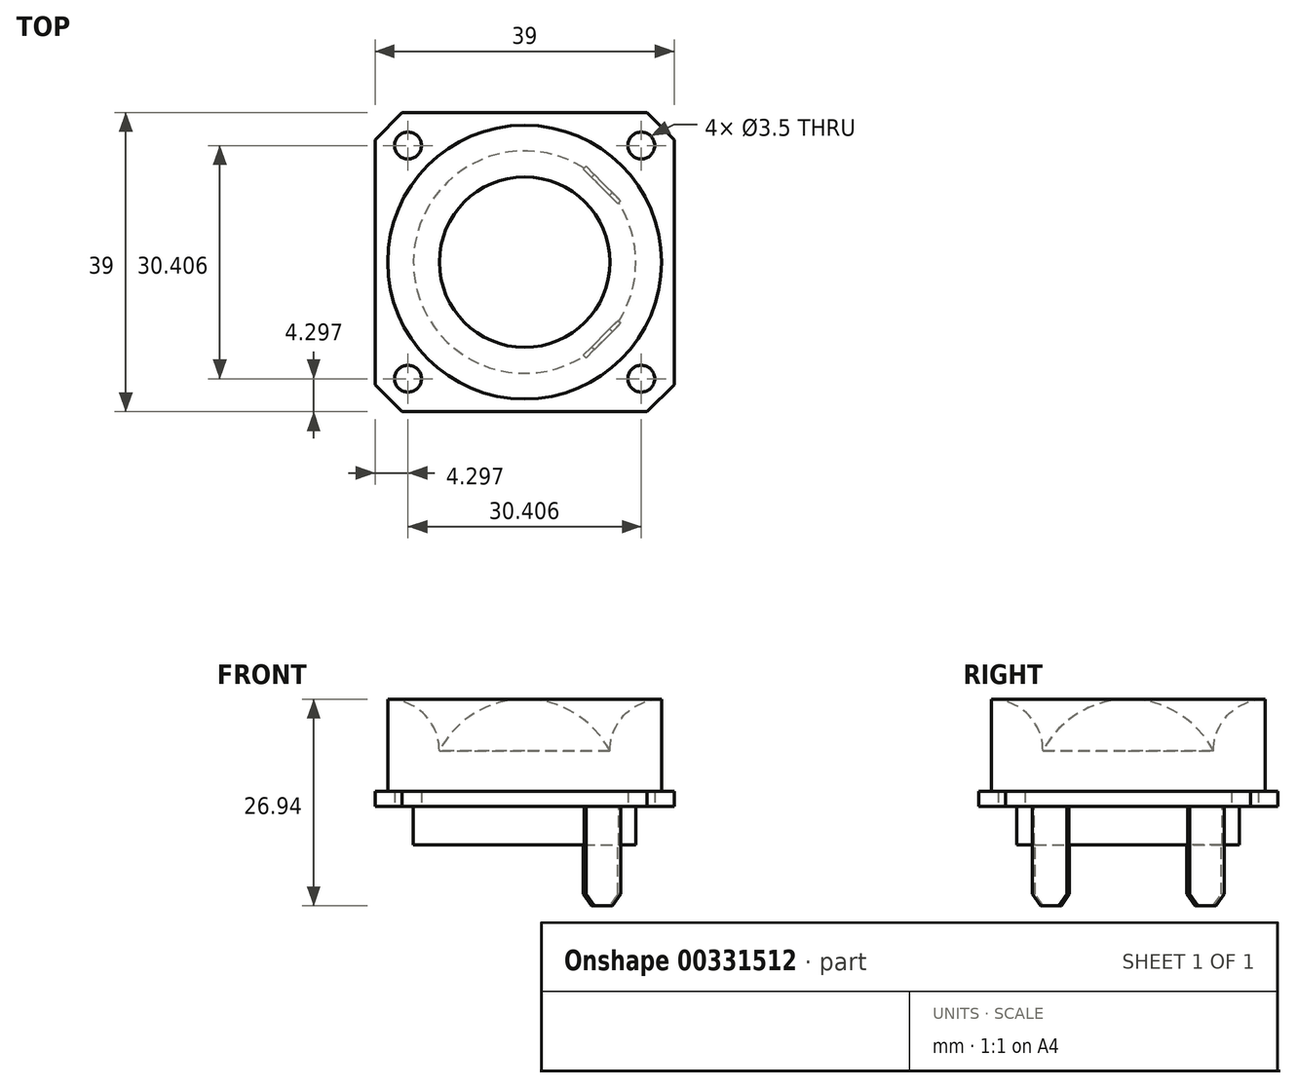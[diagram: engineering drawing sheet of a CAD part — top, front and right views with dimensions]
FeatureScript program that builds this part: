
annotation { "Feature Type Name" : "Feature", "Feature Type Description" : "" }
export const myFeature = defineFeature(function(context is Context, id is Id, definition is map)
    precondition{}
    {
        {
            var Q0;
            Q0=qCreatedBy(makeId("Right.planeOp"),FACE);
            var sketch = newSketch(context, id + "F0", { "sketchPlane" : qUnion([Q0])});
            skLineSegment(sketch, "E0", {"start": v(0, 0) * mm, "end": v(0, 18.25) * mm, "construction": true});
            skLineSegment(sketch, "E1", {"start": v(-17.85, 0) * mm, "end": v(-17.85, -14) * mm});
            skLineSegment(sketch, "E2", {"start": v(-17.85, -14) * mm, "end": v(0, -14) * mm});
            skLineSegment(sketch, "E3", {"start": v(0, -14) * mm, "end": v(0, 0) * mm});
            skArc(sketch, "E4", {"start": v(0, 0) * mm, "mid": v(-6.5, -1.82) * mm, "end": v(-11.11, -6.74) * mm});
            skArc(sketch, "E5", {"start": v(-11.11, -6.74) * mm, "mid": v(-13.09, -1.97) * mm, "end": v(-17.85, 0) * mm});
            skPoint(sketch, "E6", {"position": v(-17.85, -7) * mm});
            skSolve(sketch);
        }
        {
            var Q0;
            Q0 = qSketchRegion(id + "F0", true);
            var Q1;
            Q1=sQuery(id+"F0.wireOp",EDGE,"E0");
            revolve(context, id + "F1", {"entities" : qUnion([Q0]), "axis" : qUnion([Q1]), "revolveType" : RevolveType.FULL});
        }
        {
            var Q0;
            Q0=makeQuery(id+"F1.opRevolve","SWEPT_FACE",FACE,{"disambiguationData":[OSD([sQuery(id+"F0.wireOp",EDGE,"E2")])]});
            var sketch = newSketch(context, id + "F2", { "sketchPlane" : qUnion([Q0])});
            skLineSegment(sketch, "E7", {"start": v(0, -19.5) * mm, "end": v(15.96, -19.5) * mm});
            skLineSegment(sketch, "E8", {"start": v(15.96, -19.5) * mm, "end": v(19.5, -15.96) * mm});
            skLineSegment(sketch, "E9", {"start": v(19.5, -15.96) * mm, "end": v(19.5, 0) * mm});
            skLineSegment(sketch, "E10", {"start": v(0, 0) * mm, "end": v(0, -19.5) * mm, "construction": true});
            skLineSegment(sketch, "E11", {"start": v(0, 0) * mm, "end": v(19.5, 0) * mm, "construction": true});
            skCircle(sketch, "E12", {"center": v(15.2, -15.2) * mm, "radius": 1.75 * mm});
            skLineSegment(sketch, "E13", {"start": v(15.2, -15.2) * mm, "end": v(0, 0) * mm, "construction": true});
            skLineSegment(sketch, "E14", {"start": v(15.2, -15.2) * mm, "end": v(17.73, -17.73) * mm, "construction": true});
            skCircle(sketch, "E15.MirrorC", {"center": v(-15.2, -15.2) * mm, "radius": 1.75 * mm});
            skLineSegment(sketch, "E16.MirrorCS", {"start": v(-19.5, -15.96) * mm, "end": v(-19.5, 0) * mm});
            skLineSegment(sketch, "E17.MirrorCS", {"start": v(-15.96, -19.5) * mm, "end": v(-19.5, -15.96) * mm});
            skLineSegment(sketch, "E18.MirrorCS", {"start": v(0, -19.5) * mm, "end": v(-15.96, -19.5) * mm});
            skLineSegment(sketch, "E19.MirrorCS", {"start": v(19.5, 15.96) * mm, "end": v(19.5, 0) * mm});
            skCircle(sketch, "E20.MirrorC", {"center": v(15.2, 15.2) * mm, "radius": 1.75 * mm});
            skLineSegment(sketch, "E21.MirrorCS", {"start": v(15.96, 19.5) * mm, "end": v(19.5, 15.96) * mm});
            skLineSegment(sketch, "E22.MirrorCS", {"start": v(0, 19.5) * mm, "end": v(15.96, 19.5) * mm});
            skCircle(sketch, "E23.MirrorC", {"center": v(-15.2, 15.2) * mm, "radius": 1.75 * mm});
            skLineSegment(sketch, "E24.MirrorCS", {"start": v(-19.5, 15.96) * mm, "end": v(-19.5, 0) * mm});
            skLineSegment(sketch, "E25.MirrorCS", {"start": v(-15.96, 19.5) * mm, "end": v(-19.5, 15.96) * mm});
            skLineSegment(sketch, "E26.MirrorCS", {"start": v(0, 19.5) * mm, "end": v(-15.96, 19.5) * mm});
            skSolve(sketch);
        }
        {
            var Q0;
            Q0 = qSketchRegion(id + "F2", true);
            extrude(context, id + "F3", {"entities" : qUnion([Q0]), "operationType" : NewBodyOperationType.ADD, "oppositeDirection" : true, "depth" : 2 * mm});
        }
        {
            var Q0;
            Q0=makeQuery(id+"F3.boolean.opBoolean","MERGE",FACE,{"derivedFrom":[makeQuery(id+"F1.opRevolve","SWEPT_FACE",FACE,{"disambiguationData":[OSD([sQuery(id+"F0.wireOp",EDGE,"E2")])]}),makeQuery(id+"F3.opExtrude","CAP_FACE",FACE,{"disambiguationData":[OSD([sQuery(id+"F2.wireOp",EDGE,"E7"),sQuery(id+"F2.wireOp",EDGE,"E8"),sQuery(id+"F2.wireOp",EDGE,"E9"),sQuery(id+"F2.wireOp",EDGE,"E12"),sQuery(id+"F2.wireOp",EDGE,"E15.MirrorC"),sQuery(id+"F2.wireOp",EDGE,"E16.MirrorCS"),sQuery(id+"F2.wireOp",EDGE,"E17.MirrorCS"),sQuery(id+"F2.wireOp",EDGE,"E18.MirrorCS"),sQuery(id+"F2.wireOp",EDGE,"E19.MirrorCS"),sQuery(id+"F2.wireOp",EDGE,"E20.MirrorC"),sQuery(id+"F2.wireOp",EDGE,"E21.MirrorCS"),sQuery(id+"F2.wireOp",EDGE,"E22.MirrorCS"),sQuery(id+"F2.wireOp",EDGE,"E23.MirrorC"),sQuery(id+"F2.wireOp",EDGE,"E24.MirrorCS"),sQuery(id+"F2.wireOp",EDGE,"E25.MirrorCS"),sQuery(id+"F2.wireOp",EDGE,"E26.MirrorCS")])],"isStart":true})]});
            var sketch = newSketch(context, id + "F4", { "sketchPlane" : qUnion([Q0])});
            skCircle(sketch, "E27", {"center": v(0, 0) * mm, "radius": 14.5 * mm});
            skSolve(sketch);
        }
        {
            var Q0;
            Q0 = qSketchRegion(id + "F4", true);
            extrude(context, id + "F5", {"entities" : qUnion([Q0]), "operationType" : NewBodyOperationType.ADD, "depth" : 5 * mm});
        }
        {
            var Q0;
            Q0=makeQuery(id+"F3.boolean.opBoolean","MERGE",FACE,{"derivedFrom":[makeQuery(id+"F1.opRevolve","SWEPT_FACE",FACE,{"disambiguationData":[OSD([sQuery(id+"F0.wireOp",EDGE,"E2")])]}),makeQuery(id+"F3.opExtrude","CAP_FACE",FACE,{"disambiguationData":[OSD([sQuery(id+"F2.wireOp",EDGE,"E7"),sQuery(id+"F2.wireOp",EDGE,"E8"),sQuery(id+"F2.wireOp",EDGE,"E9"),sQuery(id+"F2.wireOp",EDGE,"E12"),sQuery(id+"F2.wireOp",EDGE,"E15.MirrorC"),sQuery(id+"F2.wireOp",EDGE,"E16.MirrorCS"),sQuery(id+"F2.wireOp",EDGE,"E17.MirrorCS"),sQuery(id+"F2.wireOp",EDGE,"E18.MirrorCS"),sQuery(id+"F2.wireOp",EDGE,"E19.MirrorCS"),sQuery(id+"F2.wireOp",EDGE,"E20.MirrorC"),sQuery(id+"F2.wireOp",EDGE,"E21.MirrorCS"),sQuery(id+"F2.wireOp",EDGE,"E22.MirrorCS"),sQuery(id+"F2.wireOp",EDGE,"E23.MirrorC"),sQuery(id+"F2.wireOp",EDGE,"E24.MirrorCS"),sQuery(id+"F2.wireOp",EDGE,"E25.MirrorCS"),sQuery(id+"F2.wireOp",EDGE,"E26.MirrorCS")])],"isStart":true})]});
            var sketch = newSketch(context, id + "F6", { "sketchPlane" : qUnion([Q0])});
            skLineSegment(sketch, "E28", {"start": v(0, 0) * mm, "end": v(13.6, 0) * mm, "construction": true});
            skLineSegment(sketch, "E29", {"start": v(8, 12.5) * mm, "end": v(12.5, 8) * mm});
            skLineSegment(sketch, "E30", {"start": v(12.14, 7.65) * mm, "end": v(12.5, 8) * mm});
            skLineSegment(sketch, "E31", {"start": v(12.14, 7.65) * mm, "end": v(7.65, 12.14) * mm});
            skLineSegment(sketch, "E32", {"start": v(8, 12.5) * mm, "end": v(7.65, 12.14) * mm});
            skPoint(sketch, "E33", {"position": v(10.25, 10.25) * mm});
            skLineSegment(sketch, "E34.MirrorCS", {"start": v(12.14, -7.65) * mm, "end": v(12.5, -8) * mm});
            skLineSegment(sketch, "E35.MirrorCS", {"start": v(12.14, -7.65) * mm, "end": v(7.65, -12.14) * mm});
            skLineSegment(sketch, "E36.MirrorCS", {"start": v(8, -12.5) * mm, "end": v(7.65, -12.14) * mm});
            skLineSegment(sketch, "E37.MirrorCS", {"start": v(8, -12.5) * mm, "end": v(12.5, -8) * mm});
            skSolve(sketch);
        }
        {
            var Q0;
            Q0 = qSketchRegion(id + "F6", true);
            extrude(context, id + "F7", {"entities" : qUnion([Q0]), "operationType" : NewBodyOperationType.ADD, "depth" : 5 * mm + 7.94 * mm});
        }
        {
            var Q0;
            Q0=makeQuery(id+"F7.opExtrude","CAP_EDGE",EDGE,{"disambiguationData":[OSD([sQuery(id+"F6.wireOp",EDGE,"E34.MirrorCS")])],"isStart":false});
            var Q1;
            Q1=makeQuery(id+"F7.opExtrude","CAP_EDGE",EDGE,{"disambiguationData":[OSD([sQuery(id+"F6.wireOp",EDGE,"E36.MirrorCS")])],"isStart":false});
            var Q2;
            Q2=makeQuery(id+"F7.opExtrude","CAP_EDGE",EDGE,{"disambiguationData":[OSD([sQuery(id+"F6.wireOp",EDGE,"E32")])],"isStart":false});
            var Q3;
            Q3=makeQuery(id+"F7.opExtrude","CAP_EDGE",EDGE,{"disambiguationData":[OSD([sQuery(id+"F6.wireOp",EDGE,"E30")])],"isStart":false});
            chamfer(context, id + "F8", {"entities" : qUnion([Q0, Q1, Q2, Q3]), "width" : 1.5 * mm, "tangentPropagation" : true});
        }
    });
